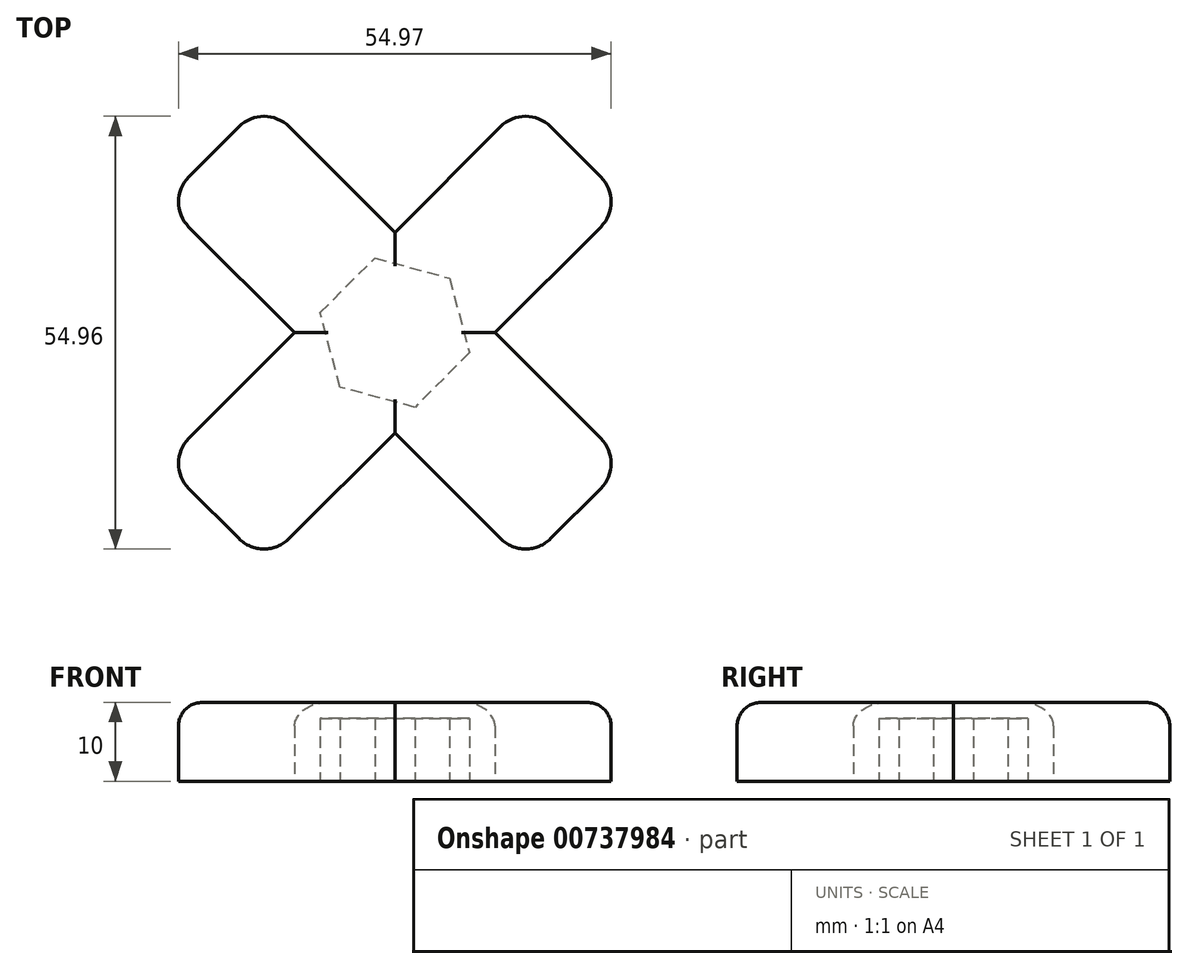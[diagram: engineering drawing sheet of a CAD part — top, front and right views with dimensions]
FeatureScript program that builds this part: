
annotation { "Feature Type Name" : "Feature", "Feature Type Description" : "" }
export const myFeature = defineFeature(function(context is Context, id is Id, definition is map)
    precondition{}
    {
        {
            var Q0;
            Q0=qCreatedBy(makeId("Top.planeOp"),FACE);
            var sketch = newSketch(context, id + "F0", { "sketchPlane" : qUnion([Q0])});
            skCircle(sketch, "E0.cCircle", {"center": v(20.34, -15.88) * mm, "radius": 9.81 * mm, "construction": true});
            skLineSegment(sketch, "E0.0", {"start": v(27.29, -8.94) * mm, "end": v(29.83, -18.42) * mm});
            skLineSegment(sketch, "E0.1", {"start": v(29.83, -18.42) * mm, "end": v(22.89, -25.36) * mm});
            skLineSegment(sketch, "E0.2", {"start": v(22.89, -25.36) * mm, "end": v(13.4, -22.82) * mm});
            skLineSegment(sketch, "E0.3", {"start": v(13.4, -22.82) * mm, "end": v(10.86, -13.34) * mm});
            skLineSegment(sketch, "E0.4", {"start": v(10.86, -13.34) * mm, "end": v(17.8, -6.4) * mm});
            skLineSegment(sketch, "E0.5", {"start": v(17.8, -6.4) * mm, "end": v(27.29, -8.94) * mm});
            skLineSegment(sketch, "E1.bottom", {"start": v(36.96, 13.46) * mm, "end": v(49.69, 0.73) * mm});
            skLineSegment(sketch, "E1.top", {"start": v(-9, -32.5) * mm, "end": v(3.73, -45.23) * mm});
            skLineSegment(sketch, "E1.left", {"start": v(36.96, 13.46) * mm, "end": v(-9, -32.5) * mm});
            skLineSegment(sketch, "E1.right", {"start": v(49.69, 0.73) * mm, "end": v(3.73, -45.23) * mm});
            skLineSegment(sketch, "E2.bottom", {"start": v(3.73, 13.46) * mm, "end": v(49.69, -32.5) * mm});
            skLineSegment(sketch, "E2.top", {"start": v(-9, 0.73) * mm, "end": v(36.96, -45.23) * mm});
            skLineSegment(sketch, "E2.left", {"start": v(3.73, 13.46) * mm, "end": v(-9, 0.73) * mm});
            skLineSegment(sketch, "E2.right", {"start": v(49.69, -32.5) * mm, "end": v(36.96, -45.23) * mm});
            skSolve(sketch);
        }
        {
            var Q0;
            Q0 = qSketchRegion(id + "F0", true);
            var Q1;
            {var subQ3=sQuery(id+"F0.wireOp",EDGE,"E2.bottom");var subQ5=sQuery(id+"F0.wireOp",EDGE,"E0.0");var subQ6=makeQuery(id+"F0.imprint","INTERSECT",VERTEX,{"derivedFrom":[subQ5,subQ3]});Q1=makeQuery(id+"F0.imprint","IMPRINT",FACE,{"disambiguationData":[TD([[makeQuery(id+"F0.imprint","IMPRINT",EDGE,{"disambiguationData":[TD([[subQ6,-1.0]])],"derivedFrom":subQ5}),-1.0]])]});}
            var Q2;
            {var subQ0=sQuery(id+"F0.wireOp",EDGE,"E0.4");Q2=makeQuery(id+"F0.imprint","IMPRINT",FACE,{"disambiguationData":[TD([[makeQuery(id+"F0.imprint","IMPRINT",EDGE,{"derivedFrom":subQ0}),-1.0]])]});}
            var Q3;
            {var subQ0=sQuery(id+"F0.wireOp",EDGE,"E0.5");var subQ1=sQuery(id+"F0.wireOp",EDGE,"E0.0");var subQ2=makeQuery(id+"F0.imprint","INTERSECT",VERTEX,{"derivedFrom":[subQ1,subQ0]});Q3=makeQuery(id+"F0.imprint","IMPRINT",FACE,{"disambiguationData":[TD([[makeQuery(id+"F0.imprint","IMPRINT",EDGE,{"disambiguationData":[TD([[subQ2,-1.0]])],"derivedFrom":subQ1}),-1.0]])]});}
            var Q4;
            {var subQ0=sQuery(id+"F0.wireOp",EDGE,"E0.1");Q4=makeQuery(id+"F0.imprint","IMPRINT",FACE,{"disambiguationData":[TD([[makeQuery(id+"F0.imprint","IMPRINT",EDGE,{"derivedFrom":subQ0}),-1.0]])]});}
            var Q5;
            {var subQ0=sQuery(id+"F0.wireOp",EDGE,"E0.3");var subQ1=sQuery(id+"F0.wireOp",EDGE,"E0.2");var subQ2=makeQuery(id+"F0.imprint","INTERSECT",VERTEX,{"derivedFrom":[subQ1,subQ0]});Q5=makeQuery(id+"F0.imprint","IMPRINT",FACE,{"disambiguationData":[TD([[makeQuery(id+"F0.imprint","IMPRINT",EDGE,{"disambiguationData":[TD([[subQ2,1.0]])],"derivedFrom":subQ1}),-1.0]])]});}
            extrude(context, id + "F1", {"entities" : qUnion([Q0, Q1, Q2, Q3, Q4, Q5]), "depth" : 10 * mm, "offsetDistance" : 25 * mm});
        }
        {
            var Q0;
            {var subQ3=sQuery(id+"F0.wireOp",EDGE,"E2.bottom");var subQ5=sQuery(id+"F0.wireOp",EDGE,"E0.0");var subQ6=makeQuery(id+"F0.imprint","INTERSECT",VERTEX,{"derivedFrom":[subQ5,subQ3]});Q0=makeQuery(id+"F0.imprint","IMPRINT",FACE,{"disambiguationData":[TD([[makeQuery(id+"F0.imprint","IMPRINT",EDGE,{"disambiguationData":[TD([[subQ6,-1.0]])],"derivedFrom":subQ5}),-1.0]])]});}
            var Q1;
            {var subQ0=sQuery(id+"F0.wireOp",EDGE,"E0.4");Q1=makeQuery(id+"F0.imprint","IMPRINT",FACE,{"disambiguationData":[TD([[makeQuery(id+"F0.imprint","IMPRINT",EDGE,{"derivedFrom":subQ0}),-1.0]])]});}
            var Q2;
            {var subQ0=sQuery(id+"F0.wireOp",EDGE,"E0.3");var subQ1=sQuery(id+"F0.wireOp",EDGE,"E0.2");var subQ2=makeQuery(id+"F0.imprint","INTERSECT",VERTEX,{"derivedFrom":[subQ1,subQ0]});Q2=makeQuery(id+"F0.imprint","IMPRINT",FACE,{"disambiguationData":[TD([[makeQuery(id+"F0.imprint","IMPRINT",EDGE,{"disambiguationData":[TD([[subQ2,1.0]])],"derivedFrom":subQ1}),-1.0]])]});}
            var Q3;
            {var subQ0=sQuery(id+"F0.wireOp",EDGE,"E0.1");Q3=makeQuery(id+"F0.imprint","IMPRINT",FACE,{"disambiguationData":[TD([[makeQuery(id+"F0.imprint","IMPRINT",EDGE,{"derivedFrom":subQ0}),-1.0]])]});}
            var Q4;
            {var subQ0=sQuery(id+"F0.wireOp",EDGE,"E0.5");var subQ1=sQuery(id+"F0.wireOp",EDGE,"E0.0");var subQ2=makeQuery(id+"F0.imprint","INTERSECT",VERTEX,{"derivedFrom":[subQ1,subQ0]});Q4=makeQuery(id+"F0.imprint","IMPRINT",FACE,{"disambiguationData":[TD([[makeQuery(id+"F0.imprint","IMPRINT",EDGE,{"disambiguationData":[TD([[subQ2,-1.0]])],"derivedFrom":subQ1}),-1.0]])]});}
            extrude(context, id + "F2", {"entities" : qUnion([Q0, Q1, Q2, Q3, Q4]), "operationType" : NewBodyOperationType.REMOVE, "depth" : 8 * mm, "offsetDistance" : 25 * mm});
        }
        {
            var Q0;
            Q0=makeQuery(id+"F1.opExtrude","CAP_FACE",FACE,{"disambiguationData":[OSD([sQuery(id+"F0.wireOp",EDGE,"E1.bottom"),sQuery(id+"F0.wireOp",EDGE,"E1.top"),sQuery(id+"F0.wireOp",EDGE,"E1.left"),sQuery(id+"F0.wireOp",EDGE,"E1.right"),sQuery(id+"F0.wireOp",EDGE,"E2.bottom"),sQuery(id+"F0.wireOp",EDGE,"E2.top"),sQuery(id+"F0.wireOp",EDGE,"E2.left"),sQuery(id+"F0.wireOp",EDGE,"E2.right")])],"isStart":false});
            fillet(context, id + "F3", {"entities" : qUnion([Q0]), "radius" : 3 * mm, "tangentPropagation" : true, "allowEdgeOverflow" : false});
        }
        {
            var Q0;
            Q0=makeQuery(id+"F1.opExtrude","SWEPT_EDGE",EDGE,{"disambiguationData":[OSD([sQuery(id+"F0.wireOp",EDGE,"E1.bottom"),sQuery(id+"F0.wireOp",EDGE,"E1.left")])]});
            var Q1;
            Q1=makeQuery(id+"F1.opExtrude","SWEPT_EDGE",EDGE,{"disambiguationData":[OSD([sQuery(id+"F0.wireOp",EDGE,"E1.bottom"),sQuery(id+"F0.wireOp",EDGE,"E1.right")])]});
            var Q2;
            Q2=makeQuery(id+"F1.opExtrude","SWEPT_EDGE",EDGE,{"disambiguationData":[OSD([sQuery(id+"F0.wireOp",EDGE,"E2.bottom"),sQuery(id+"F0.wireOp",EDGE,"E2.right")])]});
            var Q3;
            Q3=makeQuery(id+"F1.opExtrude","SWEPT_EDGE",EDGE,{"disambiguationData":[OSD([sQuery(id+"F0.wireOp",EDGE,"E2.top"),sQuery(id+"F0.wireOp",EDGE,"E2.right")])]});
            var Q4;
            Q4=makeQuery(id+"F1.opExtrude","SWEPT_EDGE",EDGE,{"disambiguationData":[OSD([sQuery(id+"F0.wireOp",EDGE,"E1.top"),sQuery(id+"F0.wireOp",EDGE,"E1.right")])]});
            var Q5;
            Q5=makeQuery(id+"F1.opExtrude","SWEPT_EDGE",EDGE,{"disambiguationData":[OSD([sQuery(id+"F0.wireOp",EDGE,"E1.top"),sQuery(id+"F0.wireOp",EDGE,"E1.left")])]});
            var Q6;
            Q6=makeQuery(id+"F1.opExtrude","SWEPT_EDGE",EDGE,{"disambiguationData":[OSD([sQuery(id+"F0.wireOp",EDGE,"E2.top"),sQuery(id+"F0.wireOp",EDGE,"E2.left")])]});
            var Q7;
            Q7=makeQuery(id+"F1.opExtrude","SWEPT_EDGE",EDGE,{"disambiguationData":[OSD([sQuery(id+"F0.wireOp",EDGE,"E2.bottom"),sQuery(id+"F0.wireOp",EDGE,"E2.left")])]});
            fillet(context, id + "F4", {"entities" : qUnion([Q0, Q1, Q2, Q3, Q4, Q5, Q6, Q7]), "radius" : 4.5 * mm, "tangentPropagation" : true, "allowEdgeOverflow" : false});
        }
    });
